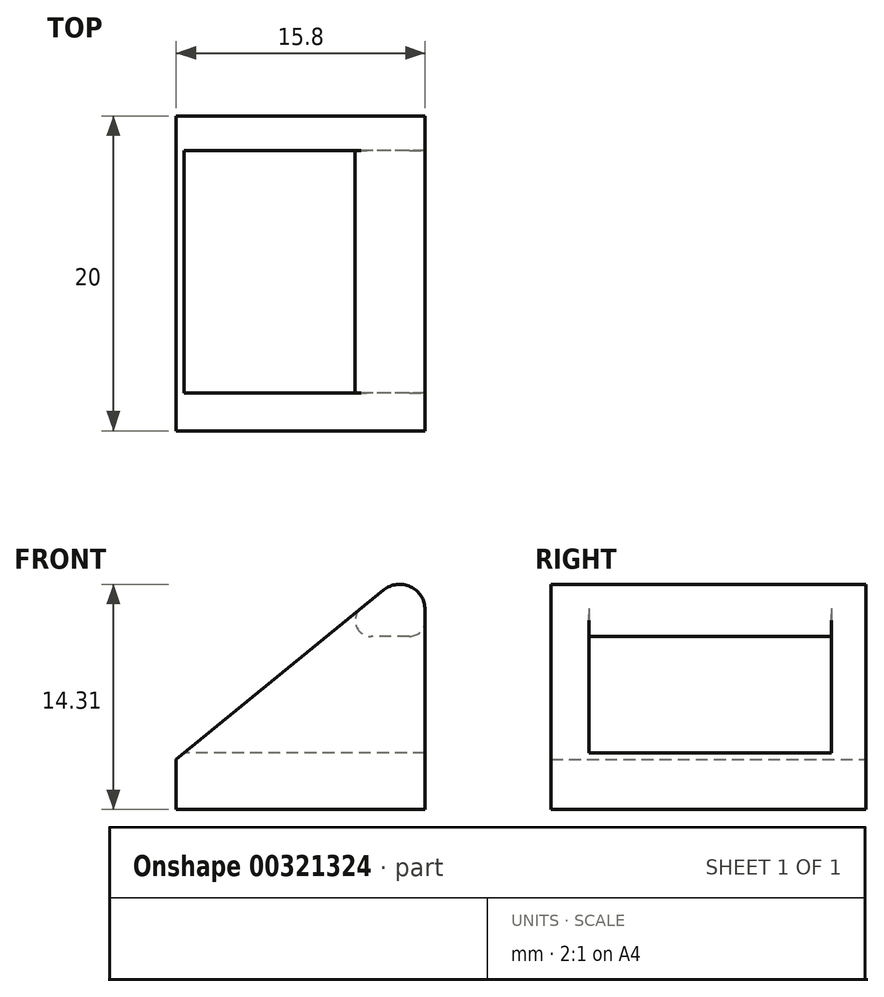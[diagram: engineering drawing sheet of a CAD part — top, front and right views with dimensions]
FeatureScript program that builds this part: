
annotation { "Feature Type Name" : "Feature", "Feature Type Description" : "" }
export const myFeature = defineFeature(function(context is Context, id is Id, definition is map)
    precondition{}
    {
        {
            var Q0;
            Q0=qCreatedBy(makeId("Front.planeOp"),FACE);
            var sketch = newSketch(context, id + "F0", { "sketchPlane" : qUnion([Q0])});
            skLineSegment(sketch, "E0", {"start": v(22.06, 0) * mm, "end": v(37.86, 0) * mm});
            skLineSegment(sketch, "E1", {"start": v(37.86, 0) * mm, "end": v(37.86, 12.7) * mm});
            skCircle(sketch, "E2", {"center": v(36.25, 12.7) * mm, "radius": 1.61 * mm});
            skLineSegment(sketch, "E3", {"start": v(22.06, 0) * mm, "end": v(22.06, 3.19) * mm});
            skLineSegment(sketch, "E4", {"start": v(22.06, 3.19) * mm, "end": v(35.23, 13.95) * mm});
            skSolve(sketch);
        }
        {
            var Q0;
            {var subQ0=sQuery(id+"F0.wireOp",EDGE,"E2");var subQ1=makeQuery(id+"F0.imprint","INTERSECT",VERTEX,{"derivedFrom":[sQuery(id+"F0.wireOp",EDGE,"E1"),subQ0]});Q0=makeQuery(id+"F0.imprint","IMPRINT",FACE,{"disambiguationData":[TD([[makeQuery(id+"F0.imprint","IMPRINT",EDGE,{"disambiguationData":[TD([[subQ1,-1.0]])],"derivedFrom":subQ0}),1.0]])]});}
            extrude(context, id + "F1", {"entities" : qUnion([Q0]), "depth" : 20 * mm});
        }
        {
            var Q0;
            Q0 = qSketchRegion(id + "F0", true);
            extrude(context, id + "F2", {"entities" : qUnion([Q0]), "operationType" : NewBodyOperationType.ADD, "depth" : 20 * mm});
        }
        {
            var Q0;
            Q0=qCreatedBy(makeId("Right.planeOp"),FACE);
            var sketch = newSketch(context, id + "F3", { "sketchPlane" : qUnion([Q0])});
            skLineSegment(sketch, "E5.bottom", {"start": v(-2.2, 3.6) * mm, "end": v(-17.6, 3.6) * mm});
            skLineSegment(sketch, "E5.top", {"start": v(-2.2, 11) * mm, "end": v(-17.6, 11) * mm});
            skLineSegment(sketch, "E5.left", {"start": v(-2.2, 3.6) * mm, "end": v(-2.2, 11) * mm});
            skLineSegment(sketch, "E5.right", {"start": v(-17.6, 3.6) * mm, "end": v(-17.6, 11) * mm});
            skSolve(sketch);
        }
        {
            var Q0;
            Q0=makeQuery(id+"F3.imprint","IMPRINT",FACE,{"disambiguationData":[TD([[makeQuery(id+"F3.imprint","IMPRINT",EDGE,{"derivedFrom":sQuery(id+"F3.wireOp",EDGE,"E5.bottom")}),-1.0]])]});
            extrude(context, id + "F4", {"entities" : qUnion([Q0]), "operationType" : NewBodyOperationType.REMOVE, "depth" : 50 * mm});
        }
        {
            var Q0;
            Q0=makeQuery(id+"F4.boolean.opBoolean","INTERSECT",EDGE,{"derivedFrom":[makeQuery(id+"F2.opExtrude","SWEPT_FACE",FACE,{"disambiguationData":[OSD([sQuery(id+"F0.wireOp",EDGE,"E4")])]}),makeQuery(id+"F4.opExtrude","SWEPT_FACE",FACE,{"disambiguationData":[OSD([sQuery(id+"F3.wireOp",EDGE,"E5.top")])]})]});
            fillet(context, id + "F5", {"entities" : qUnion([Q0]), "radius" : 1 * mm, "tangentPropagation" : true, "allowEdgeOverflow" : false});
        }
        {
            var Q0;
            Q0=makeQuery(id+"F4.boolean.opBoolean","INTERSECT",EDGE,{"derivedFrom":[makeQuery(id+"F2.opExtrude","SWEPT_FACE",FACE,{"disambiguationData":[OSD([sQuery(id+"F0.wireOp",EDGE,"E1")])]}),makeQuery(id+"F4.opExtrude","SWEPT_FACE",FACE,{"disambiguationData":[OSD([sQuery(id+"F3.wireOp",EDGE,"E5.top")])]})]});
            fillet(context, id + "F6", {"entities" : qUnion([Q0]), "radius" : 1 * mm, "tangentPropagation" : true, "allowEdgeOverflow" : false});
        }
    });
